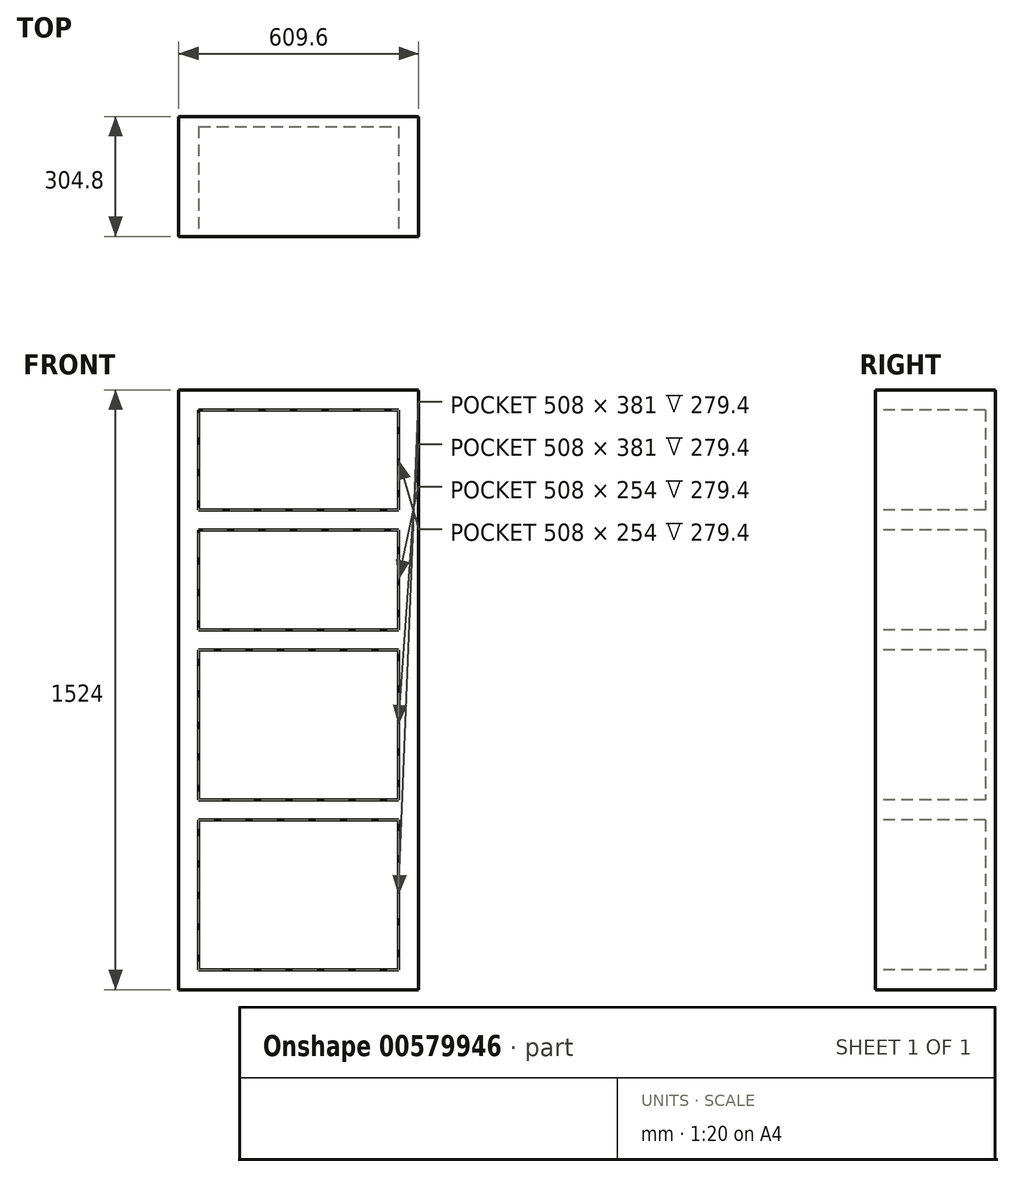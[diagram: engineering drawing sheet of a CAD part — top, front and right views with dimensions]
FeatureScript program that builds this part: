
annotation { "Feature Type Name" : "Feature", "Feature Type Description" : "" }
export const myFeature = defineFeature(function(context is Context, id is Id, definition is map)
    precondition{}
    {
        {
            var Q0;
            Q0=qCreatedBy(makeId("Top.planeOp"),FACE);
            var sketch = newSketch(context, id + "F0", { "sketchPlane" : qUnion([Q0])});
            skLineSegment(sketch, "E0.bottom", {"start": v(-420.5, 172.49) * mm, "end": v(189.1, 172.49) * mm});
            skLineSegment(sketch, "E0.top", {"start": v(-420.5, -132.31) * mm, "end": v(189.1, -132.31) * mm});
            skLineSegment(sketch, "E0.left", {"start": v(-420.5, 172.49) * mm, "end": v(-420.5, -132.31) * mm});
            skLineSegment(sketch, "E0.right", {"start": v(189.1, 172.49) * mm, "end": v(189.1, -132.31) * mm});
            skSolve(sketch);
        }
        {
            var Q0;
            Q0=makeQuery(id+"F0.imprint","IMPRINT",FACE,{"disambiguationData":[TD([[makeQuery(id+"F0.imprint","IMPRINT",EDGE,{"derivedFrom":sQuery(id+"F0.wireOp",EDGE,"E0.bottom")}),-1.0]])]});
            extrude(context, id + "F1", {"entities" : qUnion([Q0]), "depth" : 1524 * mm, "offsetDistance" : 25.4 * mm});
        }
        {
            var Q0;
            Q0=makeQuery(id+"F1.opExtrude","SWEPT_FACE",FACE,{"disambiguationData":[OSD([sQuery(id+"F0.wireOp",EDGE,"E0.top")])]});
            var sketch = newSketch(context, id + "F2", { "sketchPlane" : qUnion([Q0])});
            skLineSegment(sketch, "E1.bottom", {"start": v(-369.7, 1473.2) * mm, "end": v(138.3, 1473.2) * mm});
            skLineSegment(sketch, "E1.top", {"start": v(-369.7, 1219.2) * mm, "end": v(138.3, 1219.2) * mm});
            skLineSegment(sketch, "E1.left", {"start": v(-369.7, 1473.2) * mm, "end": v(-369.7, 1219.2) * mm});
            skLineSegment(sketch, "E1.right", {"start": v(138.3, 1473.2) * mm, "end": v(138.3, 1219.2) * mm});
            skLineSegment(sketch, "E2.bottom", {"start": v(-369.7, 1168.4) * mm, "end": v(138.3, 1168.4) * mm});
            skLineSegment(sketch, "E2.top", {"start": v(-369.7, 914.4) * mm, "end": v(138.3, 914.4) * mm});
            skLineSegment(sketch, "E2.left", {"start": v(-369.7, 1168.4) * mm, "end": v(-369.7, 914.4) * mm});
            skLineSegment(sketch, "E2.right", {"start": v(138.3, 1168.4) * mm, "end": v(138.3, 914.4) * mm});
            skLineSegment(sketch, "E3.bottom", {"start": v(-369.7, 863.6) * mm, "end": v(138.3, 863.6) * mm});
            skLineSegment(sketch, "E3.top", {"start": v(-369.7, 482.6) * mm, "end": v(138.3, 482.6) * mm});
            skLineSegment(sketch, "E3.left", {"start": v(-369.7, 863.6) * mm, "end": v(-369.7, 482.6) * mm});
            skLineSegment(sketch, "E3.right", {"start": v(138.3, 863.6) * mm, "end": v(138.3, 482.6) * mm});
            skLineSegment(sketch, "E4.bottom", {"start": v(-369.7, 431.8) * mm, "end": v(138.3, 431.8) * mm});
            skLineSegment(sketch, "E4.top", {"start": v(-369.7, 50.8) * mm, "end": v(138.3, 50.8) * mm});
            skLineSegment(sketch, "E4.left", {"start": v(-369.7, 431.8) * mm, "end": v(-369.7, 50.8) * mm});
            skLineSegment(sketch, "E4.right", {"start": v(138.3, 431.8) * mm, "end": v(138.3, 50.8) * mm});
            skSolve(sketch);
        }
        {
            var Q0;
            Q0 = qSketchRegion(id + "F2", true);
            extrude(context, id + "F3", {"entities" : qUnion([Q0]), "operationType" : NewBodyOperationType.REMOVE, "oppositeDirection" : true, "depth" : 279.4 * mm, "offsetDistance" : 25.4 * mm});
        }
    });
